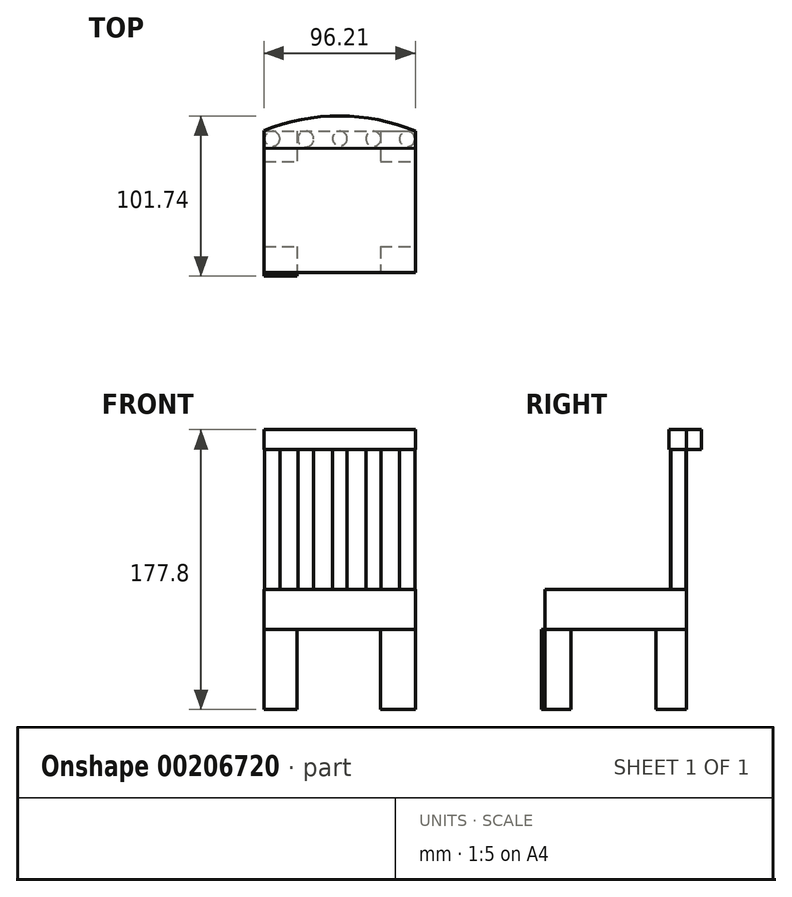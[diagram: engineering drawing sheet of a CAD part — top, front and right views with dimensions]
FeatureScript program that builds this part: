
annotation { "Feature Type Name" : "Feature", "Feature Type Description" : "" }
export const myFeature = defineFeature(function(context is Context, id is Id, definition is map)
    precondition{}
    {
        {
            var Q0;
            Q0=qCreatedBy(makeId("Top.planeOp"),FACE);
            var sketch = newSketch(context, id + "F0", { "sketchPlane" : qUnion([Q0])});
            skLineSegment(sketch, "E0.bottom", {"start": v(-50.2, 48.06) * mm, "end": v(-29.38, 48.06) * mm});
            skLineSegment(sketch, "E0.top", {"start": v(-50.2, 28.67) * mm, "end": v(-29.38, 28.67) * mm});
            skLineSegment(sketch, "E0.left", {"start": v(-50.2, 48.06) * mm, "end": v(-50.2, 28.67) * mm});
            skLineSegment(sketch, "E0.right", {"start": v(-29.38, 48.06) * mm, "end": v(-29.38, 28.67) * mm});
            skLineSegment(sketch, "E1.bottom", {"start": v(23.67, 48.06) * mm, "end": v(45.92, 48.06) * mm});
            skLineSegment(sketch, "E1.top", {"start": v(23.67, 48.06) * mm, "end": v(45.92, 48.06) * mm});
            skLineSegment(sketch, "E1.left", {"start": v(23.67, 48.06) * mm, "end": v(23.67, 48.06) * mm});
            skLineSegment(sketch, "E1.right", {"start": v(47.64, 48.06) * mm, "end": v(47.64, 48.06) * mm});
            skLineSegment(sketch, "E2.top", {"start": v(23.67, 28.67) * mm, "end": v(45.92, 28.67) * mm});
            skLineSegment(sketch, "E2.left", {"start": v(23.67, 48.06) * mm, "end": v(23.67, 28.67) * mm});
            skLineSegment(sketch, "E2.right", {"start": v(45.92, 48.06) * mm, "end": v(45.92, 28.67) * mm});
            skLineSegment(sketch, "E3.bottom", {"start": v(-50.2, -25.24) * mm, "end": v(-29.38, -25.24) * mm});
            skLineSegment(sketch, "E3.top", {"start": v(-50.2, -44.07) * mm, "end": v(-29.38, -44.07) * mm});
            skLineSegment(sketch, "E3.left", {"start": v(-50.2, -25.24) * mm, "end": v(-50.2, -44.07) * mm});
            skLineSegment(sketch, "E3.right", {"start": v(-29.38, -25.24) * mm, "end": v(-29.38, -44.07) * mm});
            skLineSegment(sketch, "E4.bottom", {"start": v(23.67, -25.24) * mm, "end": v(45.92, -25.24) * mm});
            skLineSegment(sketch, "E4.top", {"start": v(23.67, -41.79) * mm, "end": v(45.92, -41.79) * mm});
            skLineSegment(sketch, "E4.left", {"start": v(23.67, -25.24) * mm, "end": v(23.67, -41.79) * mm});
            skLineSegment(sketch, "E4.right", {"start": v(45.92, -25.24) * mm, "end": v(45.92, -41.79) * mm});
            skSolve(sketch);
        }
        {
            var Q0;
            Q0=makeQuery(id+"F0.imprint","IMPRINT",FACE,{"disambiguationData":[TD([[makeQuery(id+"F0.imprint","IMPRINT",EDGE,{"derivedFrom":sQuery(id+"F0.wireOp",EDGE,"E0.bottom")}),-1.0]])]});
            var Q1;
            Q1=makeQuery(id+"F0.imprint","IMPRINT",FACE,{"disambiguationData":[TD([[makeQuery(id+"F0.imprint","IMPRINT",EDGE,{"derivedFrom":sQuery(id+"F0.wireOp",EDGE,"E1.bottom")}),-1.0]])]});
            var Q2;
            Q2=makeQuery(id+"F0.imprint","IMPRINT",FACE,{"disambiguationData":[TD([[makeQuery(id+"F0.imprint","IMPRINT",EDGE,{"derivedFrom":sQuery(id+"F0.wireOp",EDGE,"E4.bottom")}),-1.0]])]});
            var Q3;
            Q3=makeQuery(id+"F0.imprint","IMPRINT",FACE,{"disambiguationData":[TD([[makeQuery(id+"F0.imprint","IMPRINT",EDGE,{"derivedFrom":sQuery(id+"F0.wireOp",EDGE,"E3.bottom")}),-1.0]])]});
            extrude(context, id + "F1", {"entities" : qUnion([Q0, Q1, Q2, Q3]), "depth" : 50.8 * mm});
        }
        {
            var Q0;
            Q0=makeQuery(id+"F1.opExtrude","CAP_FACE",FACE,{"disambiguationData":[OSD([sQuery(id+"F0.wireOp",EDGE,"E0.bottom"),sQuery(id+"F0.wireOp",EDGE,"E0.top"),sQuery(id+"F0.wireOp",EDGE,"E0.left"),sQuery(id+"F0.wireOp",EDGE,"E0.right")])],"isStart":false});
            var sketch = newSketch(context, id + "F2", { "sketchPlane" : qUnion([Q0])});
            skLineSegment(sketch, "E5.bottom", {"start": v(-50.2, 48.06) * mm, "end": v(45.92, 48.06) * mm});
            skLineSegment(sketch, "E5.top", {"start": v(-50.2, -41.79) * mm, "end": v(45.92, -41.79) * mm});
            skLineSegment(sketch, "E5.left", {"start": v(-50.2, 48.06) * mm, "end": v(-50.2, -41.79) * mm});
            skLineSegment(sketch, "E5.right", {"start": v(45.92, 48.06) * mm, "end": v(45.92, -41.79) * mm});
            skSolve(sketch);
        }
        {
            var Q0;
            {var subQ3=sQuery(id+"F2.wireOp",EDGE,"E5.top");Q0=makeQuery(id+"F2.imprint","IMPRINT",FACE,{"disambiguationData":[TD([[makeQuery(id+"F2.imprint","IMPRINT",EDGE,{"derivedFrom":subQ3}),1.0]])]});}
            var Q1;
            {var subQ4=makeQuery(id+"F1.opExtrude","CAP_EDGE",EDGE,{"disambiguationData":[OSD([sQuery(id+"F0.wireOp",EDGE,"E0.top")])],"isStart":false});Q1=makeQuery(id+"F2.imprint","IMPRINT",FACE,{"disambiguationData":[TD([[makeQuery(id+"F2.imprint","IMPRINT",EDGE,{"derivedFrom":subQ4}),1.0]])]});}
            extrude(context, id + "F3", {"entities" : qUnion([Q0, Q1]), "depth" : 25.4 * mm});
        }
        {
            var Q0;
            Q0=makeQuery(id+"F3.opExtrude","CAP_FACE",FACE,{"disambiguationData":[OSD([sQuery(id+"F2.wireOp",EDGE,"E5.bottom"),sQuery(id+"F2.wireOp",EDGE,"E5.top"),sQuery(id+"F2.wireOp",EDGE,"E5.left"),sQuery(id+"F2.wireOp",EDGE,"E5.right")])],"isStart":false});
            var sketch = newSketch(context, id + "F4", { "sketchPlane" : qUnion([Q0])});
            skCircle(sketch, "E6", {"center": v(-45.02, 43.19) * mm, "radius": 4.86 * mm});
            skCircle(sketch, "E7", {"center": v(-23.67, 43) * mm, "radius": 5.03 * mm});
            skCircle(sketch, "E8", {"center": v(-2.02, 43.33) * mm, "radius": 4.63 * mm});
            skCircle(sketch, "E9", {"center": v(19.27, 43.19) * mm, "radius": 4.76 * mm});
            skCircle(sketch, "E10", {"center": v(40.7, 43.05) * mm, "radius": 4.86 * mm});
            skSolve(sketch);
        }
        {
            var Q0;
            Q0=makeQuery(id+"F4.imprint","IMPRINT",FACE,{"disambiguationData":[TD([[makeQuery(id+"F4.imprint","IMPRINT",EDGE,{"derivedFrom":sQuery(id+"F4.wireOp",EDGE,"E6")}),1.0]])]});
            var Q1;
            Q1=makeQuery(id+"F4.imprint","IMPRINT",FACE,{"disambiguationData":[TD([[makeQuery(id+"F4.imprint","IMPRINT",EDGE,{"derivedFrom":sQuery(id+"F4.wireOp",EDGE,"E9")}),1.0]])]});
            var Q2;
            Q2=makeQuery(id+"F4.imprint","IMPRINT",FACE,{"disambiguationData":[TD([[makeQuery(id+"F4.imprint","IMPRINT",EDGE,{"derivedFrom":sQuery(id+"F4.wireOp",EDGE,"E10")}),1.0]])]});
            var Q3;
            Q3=makeQuery(id+"F4.imprint","IMPRINT",FACE,{"disambiguationData":[TD([[makeQuery(id+"F4.imprint","IMPRINT",EDGE,{"derivedFrom":sQuery(id+"F4.wireOp",EDGE,"E8")}),1.0]])]});
            var Q4;
            Q4=makeQuery(id+"F4.imprint","IMPRINT",FACE,{"disambiguationData":[TD([[makeQuery(id+"F4.imprint","IMPRINT",EDGE,{"derivedFrom":sQuery(id+"F4.wireOp",EDGE,"E7")}),1.0]])]});
            extrude(context, id + "F5", {"entities" : qUnion([Q0, Q1, Q2, Q3, Q4]), "operationType" : NewBodyOperationType.ADD, "depth" : 88.9 * mm});
        }
        {
            var Q0;
            Q0=makeQuery(id+"F5.opExtrude","CAP_FACE",FACE,{"disambiguationData":[OSD([sQuery(id+"F4.wireOp",EDGE,"E6")])],"isStart":false});
            var sketch = newSketch(context, id + "F6", { "sketchPlane" : qUnion([Q0])});
            skArc(sketch, "E11", {"start": v(45.88, 48.05) * mm, "mid": v(-2.16, 57.67) * mm, "end": v(-50.29, 48.5) * mm});
            skLineSegment(sketch, "E12", {"start": v(-50.29, 37.21) * mm, "end": v(45.88, 37.06) * mm});
            skLineSegment(sketch, "E13", {"start": v(-50.29, 48.5) * mm, "end": v(-50.29, 37.21) * mm});
            skLineSegment(sketch, "E14", {"start": v(45.88, 48.05) * mm, "end": v(45.88, 37.06) * mm});
            skSolve(sketch);
        }
        {
            var Q0;
            Q0=makeQuery(id+"F6.imprint","IMPRINT",FACE,{"disambiguationData":[TD([[makeQuery(id+"F6.imprint","IMPRINT",EDGE,{"derivedFrom":sQuery(id+"F6.wireOp",EDGE,"E11")}),1.0]])]});
            var Q1;
            Q1=makeQuery(id+"F6.imprint","IMPRINT",FACE,{"disambiguationData":[TD([[makeQuery(id+"F6.imprint","IMPRINT",EDGE,{"derivedFrom":makeQuery(id+"F5.opExtrude","CAP_EDGE",EDGE,{"disambiguationData":[OSD([sQuery(id+"F4.wireOp",EDGE,"E6")])],"isStart":false})}),1.0]])]});
            extrude(context, id + "F7", {"entities" : qUnion([Q0, Q1]), "depth" : 12.7 * mm});
        }
    });
